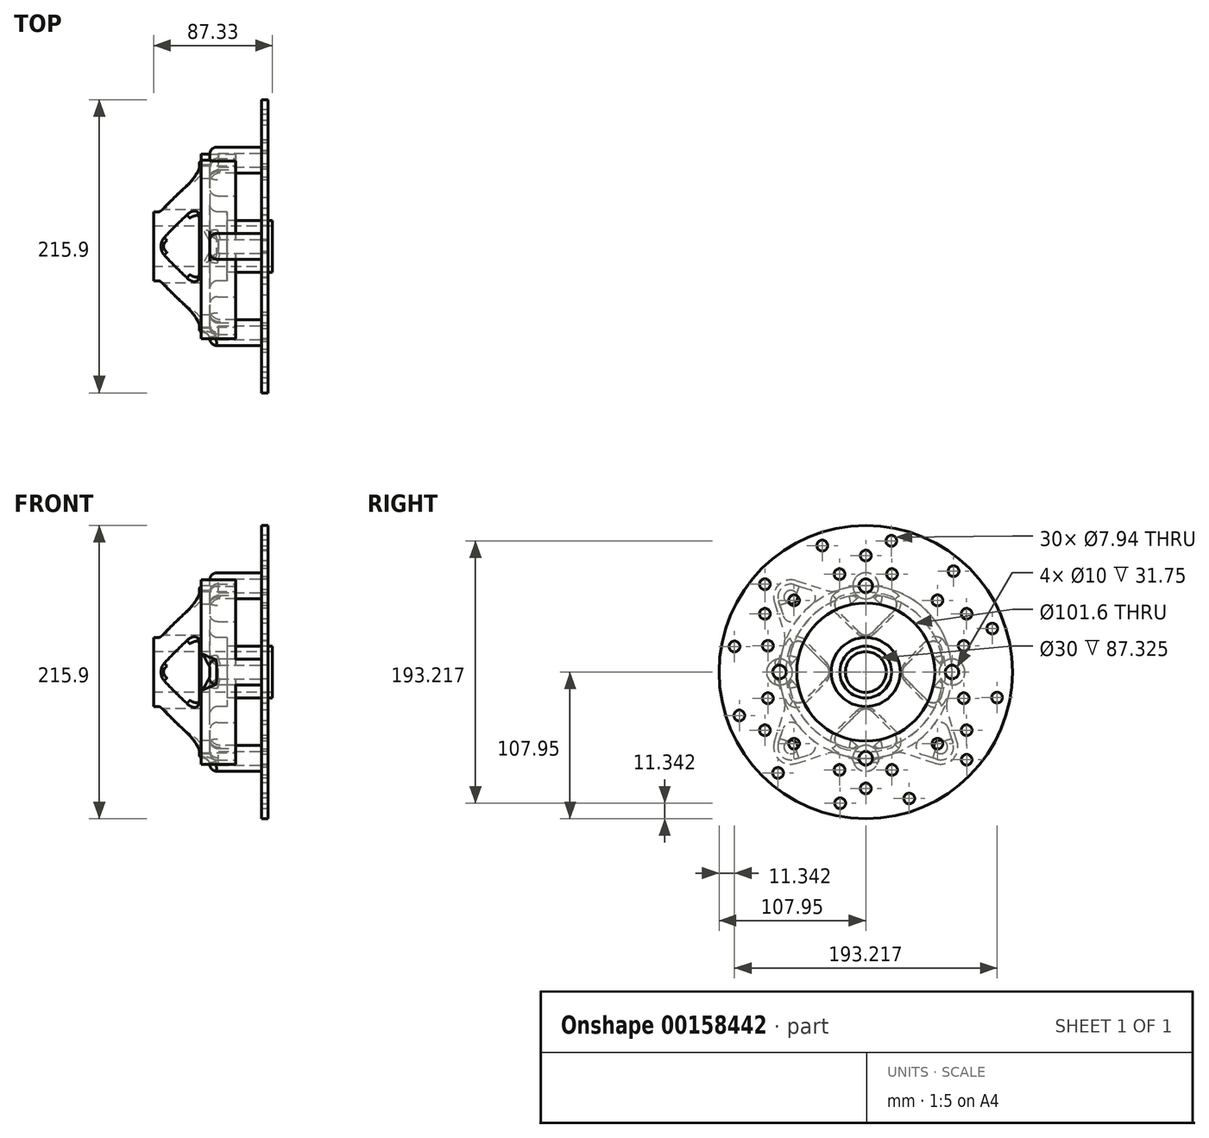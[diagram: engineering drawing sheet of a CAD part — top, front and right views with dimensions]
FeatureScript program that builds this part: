
annotation { "Feature Type Name" : "Feature", "Feature Type Description" : "" }
export const myFeature = defineFeature(function(context is Context, id is Id, definition is map)
    precondition{}
    {
        {
            var Q0;
            Q0=qCreatedBy(makeId("Front.planeOp"),FACE);
            var sketch = newSketch(context, id + "F0", { "sketchPlane" : qUnion([Q0])});
            skLineSegment(sketch, "E0", {"start": v(0, 15) * mm, "end": v(0, 25.4) * mm});
            skLineSegment(sketch, "E1", {"start": v(0, 25.4) * mm, "end": v(4.78, 25.4) * mm});
            skLineSegment(sketch, "E2", {"start": v(4.78, 25.4) * mm, "end": v(34.95, 63.5) * mm});
            skLineSegment(sketch, "E3", {"start": v(34.95, 63.5) * mm, "end": v(60.35, 63.5) * mm});
            skLineSegment(sketch, "E4", {"start": v(60.35, 63.5) * mm, "end": v(60.35, 57.15) * mm});
            skLineSegment(sketch, "E5", {"start": v(60.35, 57.15) * mm, "end": v(41.3, 57.15) * mm});
            skLineSegment(sketch, "E6", {"start": v(41.3, 57.15) * mm, "end": v(41.3, 25.4) * mm});
            skLineSegment(sketch, "E7", {"start": v(41.3, 25.4) * mm, "end": v(54, 25.4) * mm});
            skLineSegment(sketch, "E8", {"start": v(54, 25.4) * mm, "end": v(54, 19.05) * mm});
            skLineSegment(sketch, "E9", {"start": v(54, 19.05) * mm, "end": v(87.33, 19.05) * mm});
            skLineSegment(sketch, "E10", {"start": v(87.33, 19.05) * mm, "end": v(87.33, 15) * mm});
            skLineSegment(sketch, "E11", {"start": v(87.33, 15) * mm, "end": v(0, 15) * mm});
            skLineSegment(sketch, "E12", {"start": v(0, 0) * mm, "end": v(87.33, 0) * mm, "construction": true});
            skSolve(sketch);
        }
        {
            var Q0;
            Q0 = qSketchRegion(id + "F0", true);
            var Q1;
            Q1=sQuery(id+"F0.wireOp",EDGE,"E12");
            revolve(context, id + "F1", {"entities" : qUnion([Q0]), "axis" : qUnion([Q1]), "revolveType" : RevolveType.FULL});
        }
        {
            var Q0;
            Q0=makeQuery(id+"F1.opRevolve","SWEPT_FACE",FACE,{"disambiguationData":[OSD([sQuery(id+"F0.wireOp",EDGE,"E4")])]});
            var sketch = newSketch(context, id + "F2", { "sketchPlane" : qUnion([Q0])});
            skLineSegment(sketch, "E13", {"start": v(-55.15, 55.15) * mm, "end": v(55.15, 55.15) * mm, "construction": true});
            skLineSegment(sketch, "E14", {"start": v(55.15, -55.15) * mm, "end": v(55.15, 55.15) * mm, "construction": true});
            skPoint(sketch, "E15", {"position": v(55.15, 0) * mm});
            skPoint(sketch, "E16", {"position": v(0, 55.15) * mm});
            skCircle(sketch, "E17.0", {"center": v(0, 0) * mm, "radius": 63.5 * mm});
            skArc(sketch, "E18", {"start": v(51.29, 67.25) * mm, "mid": v(64.13, 64.13) * mm, "end": v(67.25, 51.29) * mm});
            skCircle(sketch, "E19", {"center": v(55.15, 55.15) * mm, "radius": 5 * mm});
            skLineSegment(sketch, "E20", {"start": v(51.29, 67.25) * mm, "end": v(28.56, 60) * mm});
            skArc(sketch, "E21", {"start": v(28.56, 60) * mm, "mid": v(24.56, 59.39) * mm, "end": v(20.58, 60.07) * mm});
            skLineSegment(sketch, "E22", {"start": v(67.25, 51.29) * mm, "end": v(60, 28.56) * mm});
            skArc(sketch, "E23", {"start": v(60, 28.56) * mm, "mid": v(59.39, 24.56) * mm, "end": v(60.07, 20.58) * mm});
            skArc(sketch, "E24.1.0", {"start": v(28.56, -60) * mm, "mid": v(24.56, -59.39) * mm, "end": v(20.58, -60.07) * mm});
            skArc(sketch, "E24.1.1", {"start": v(67.25, -51.29) * mm, "mid": v(64.13, -64.13) * mm, "end": v(51.29, -67.25) * mm});
            skLineSegment(sketch, "E24.1.2", {"start": v(67.25, -51.29) * mm, "end": v(60, -28.56) * mm});
            skArc(sketch, "E24.1.3", {"start": v(60, -28.56) * mm, "mid": v(59.39, -24.56) * mm, "end": v(60.07, -20.58) * mm});
            skCircle(sketch, "E24.1.4", {"center": v(55.15, -55.15) * mm, "radius": 5 * mm});
            skLineSegment(sketch, "E24.1.5", {"start": v(51.29, -67.25) * mm, "end": v(28.56, -60) * mm});
            skArc(sketch, "E24.2.0", {"start": v(-60, -28.56) * mm, "mid": v(-59.39, -24.56) * mm, "end": v(-60.07, -20.58) * mm});
            skArc(sketch, "E24.2.1", {"start": v(-51.29, -67.25) * mm, "mid": v(-64.13, -64.13) * mm, "end": v(-67.25, -51.29) * mm});
            skLineSegment(sketch, "E24.2.2", {"start": v(-51.29, -67.25) * mm, "end": v(-28.56, -60) * mm});
            skArc(sketch, "E24.2.3", {"start": v(-28.56, -60) * mm, "mid": v(-24.56, -59.39) * mm, "end": v(-20.58, -60.07) * mm});
            skCircle(sketch, "E24.2.4", {"center": v(-55.15, -55.15) * mm, "radius": 5 * mm});
            skLineSegment(sketch, "E24.2.5", {"start": v(-67.25, -51.29) * mm, "end": v(-60, -28.56) * mm});
            skArc(sketch, "E24.3.0", {"start": v(-28.56, 60) * mm, "mid": v(-24.56, 59.39) * mm, "end": v(-20.58, 60.07) * mm});
            skArc(sketch, "E24.3.1", {"start": v(-67.25, 51.29) * mm, "mid": v(-64.13, 64.13) * mm, "end": v(-51.29, 67.25) * mm});
            skLineSegment(sketch, "E24.3.2", {"start": v(-67.25, 51.29) * mm, "end": v(-60, 28.56) * mm});
            skArc(sketch, "E24.3.3", {"start": v(-60, 28.56) * mm, "mid": v(-59.39, 24.56) * mm, "end": v(-60.07, 20.58) * mm});
            skCircle(sketch, "E24.3.4", {"center": v(-55.15, 55.15) * mm, "radius": 5 * mm});
            skLineSegment(sketch, "E24.3.5", {"start": v(-51.29, 67.25) * mm, "end": v(-28.56, 60) * mm});
            skLineSegment(sketch, "E24.anchor1", {"start": v(0, 0) * mm, "end": v(60.07, 20.58) * mm, "construction": true});
            skLineSegment(sketch, "E24.anchor2", {"start": v(0, 0) * mm, "end": v(-20.58, 60.07) * mm, "construction": true});
            skSolve(sketch);
        }
        {
            var Q0;
            Q0=makeQuery(id+"F2.imprint","IMPRINT",FACE,{"disambiguationData":[TD([[makeQuery(id+"F2.imprint","IMPRINT",EDGE,{"derivedFrom":sQuery(id+"F2.wireOp",EDGE,"E18")}),-1.0]])]});
            var Q1;
            {var subQ0=sQuery(id+"F2.wireOp",EDGE,"E24.3.0");Q1=makeQuery(id+"F2.imprint","IMPRINT",FACE,{"disambiguationData":[TD([[makeQuery(id+"F2.imprint","IMPRINT",EDGE,{"derivedFrom":subQ0}),-1.0]])]});}
            var Q2;
            {var subQ0=sQuery(id+"F2.wireOp",EDGE,"E24.2.0");Q2=makeQuery(id+"F2.imprint","IMPRINT",FACE,{"disambiguationData":[TD([[makeQuery(id+"F2.imprint","IMPRINT",EDGE,{"derivedFrom":subQ0}),-1.0]])]});}
            var Q3;
            {var subQ1=sQuery(id+"F2.wireOp",EDGE,"E24.1.0");Q3=makeQuery(id+"F2.imprint","IMPRINT",FACE,{"disambiguationData":[TD([[makeQuery(id+"F2.imprint","IMPRINT",EDGE,{"derivedFrom":subQ1}),-1.0]])]});}
            var Q4;
            Q4=makeQuery(id+"F1.opRevolve","SWEPT_FACE",FACE,{"disambiguationData":[OSD([sQuery(id+"F0.wireOp",EDGE,"E2")])]});
            extrude(context, id + "F3", {"entities" : qUnion([Q0, Q1, Q2, Q3]), "operationType" : NewBodyOperationType.ADD, "oppositeDirection" : true, "endBoundEntityFace" : qUnion([Q4]), "depth" : 25.4 * mm});
        }
        {
            var Q0;
            Q0=makeQuery(id+"F3.opExtrude","CAP_FACE",FACE,{"disambiguationData":[OSD([sQuery(id+"F2.wireOp",EDGE,"E17.0"),sQuery(id+"F2.wireOp",EDGE,"E24.3.0"),sQuery(id+"F2.wireOp",EDGE,"E24.3.1"),sQuery(id+"F2.wireOp",EDGE,"E24.3.2"),sQuery(id+"F2.wireOp",EDGE,"E24.3.3"),sQuery(id+"F2.wireOp",EDGE,"E24.3.4"),sQuery(id+"F2.wireOp",EDGE,"E24.3.5")])],"isStart":false});
            cPlane(context, id + "F4", {"entities" : qUnion([Q0]), "cplaneType" : CPlaneType.OFFSET, "offset" : 6.35 * mm, "oppositeDirection" : true, "width" : 152.4 * mm, "height" : 152.4 * mm});
        }
        {
            var Q0;
            Q0=qCreatedBy(id+"F4.planeOp",FACE);
            var sketch = newSketch(context, id + "F5", { "sketchPlane" : qUnion([Q0])});
            skCircle(sketch, "E25", {"center": v(0, 63.5) * mm, "radius": 9.53 * mm});
            skCircle(sketch, "E26.1.0", {"center": v(-63.5, 0) * mm, "radius": 9.53 * mm});
            skCircle(sketch, "E26.2.0", {"center": v(0, -63.5) * mm, "radius": 9.53 * mm});
            skCircle(sketch, "E26.3.0", {"center": v(63.5, 0) * mm, "radius": 9.53 * mm});
            skPoint(sketch, "E26.center", {"position": v(0, 0) * mm});
            skSolve(sketch);
        }
        {
            var Q0;
            Q0 = qSketchRegion(id + "F5", true);
            extrude(context, id + "F6", {"entities" : qUnion([Q0]), "operationType" : NewBodyOperationType.ADD, "oppositeDirection" : true, "depth" : 38.1 * mm});
        }
        {
            var Q0;
            {var subQ0=sQuery(id+"F2.wireOp",EDGE,"E17.0");Q0=makeQuery(id+"F3.boolean.opBoolean","MERGE",FACE,{"derivedFrom":[makeQuery(id+"F1.opRevolve","SWEPT_FACE",FACE,{"disambiguationData":[OSD([sQuery(id+"F0.wireOp",EDGE,"E4")])]}),makeQuery(id+"F3.opExtrude","CAP_FACE",FACE,{"disambiguationData":[OSD([subQ0,sQuery(id+"F2.wireOp",EDGE,"E18"),sQuery(id+"F2.wireOp",EDGE,"E19"),sQuery(id+"F2.wireOp",EDGE,"E20"),sQuery(id+"F2.wireOp",EDGE,"E21"),sQuery(id+"F2.wireOp",EDGE,"E22"),sQuery(id+"F2.wireOp",EDGE,"E23")])],"isStart":true}),makeQuery(id+"F3.opExtrude","CAP_FACE",FACE,{"disambiguationData":[OSD([subQ0,sQuery(id+"F2.wireOp",EDGE,"E24.1.0"),sQuery(id+"F2.wireOp",EDGE,"E24.1.1"),sQuery(id+"F2.wireOp",EDGE,"E24.1.2"),sQuery(id+"F2.wireOp",EDGE,"E24.1.3"),sQuery(id+"F2.wireOp",EDGE,"E24.1.4"),sQuery(id+"F2.wireOp",EDGE,"E24.1.5")])],"isStart":true}),makeQuery(id+"F3.opExtrude","CAP_FACE",FACE,{"disambiguationData":[OSD([subQ0,sQuery(id+"F2.wireOp",EDGE,"E24.2.0"),sQuery(id+"F2.wireOp",EDGE,"E24.2.1"),sQuery(id+"F2.wireOp",EDGE,"E24.2.2"),sQuery(id+"F2.wireOp",EDGE,"E24.2.3"),sQuery(id+"F2.wireOp",EDGE,"E24.2.4"),sQuery(id+"F2.wireOp",EDGE,"E24.2.5")])],"isStart":true}),makeQuery(id+"F3.opExtrude","CAP_FACE",FACE,{"disambiguationData":[OSD([subQ0,sQuery(id+"F2.wireOp",EDGE,"E24.3.0"),sQuery(id+"F2.wireOp",EDGE,"E24.3.1"),sQuery(id+"F2.wireOp",EDGE,"E24.3.2"),sQuery(id+"F2.wireOp",EDGE,"E24.3.3"),sQuery(id+"F2.wireOp",EDGE,"E24.3.4"),sQuery(id+"F2.wireOp",EDGE,"E24.3.5")])],"isStart":true})]});}
            var sketch = newSketch(context, id + "F7", { "sketchPlane" : qUnion([Q0])});
            skLineSegment(sketch, "E27.0", {"start": v(-52.26, 64.23) * mm, "end": v(-41.47, 60.78) * mm});
            skArc(sketch, "E27.1", {"start": v(-64.23, 52.26) * mm, "mid": v(-61.89, 61.89) * mm, "end": v(-52.26, 64.23) * mm});
            skLineSegment(sketch, "E27.2", {"start": v(-64.23, 52.26) * mm, "end": v(-60.78, 41.47) * mm});
            skArc(sketch, "E28", {"start": v(-39.45, 49.76) * mm, "mid": v(-44.9, 44.9) * mm, "end": v(-49.76, 39.45) * mm});
            skArc(sketch, "E29", {"start": v(-41.47, 60.78) * mm, "mid": v(-37.15, 55.87) * mm, "end": v(-39.45, 49.76) * mm});
            skArc(sketch, "E30", {"start": v(-60.78, 41.47) * mm, "mid": v(-55.87, 37.15) * mm, "end": v(-49.76, 39.45) * mm});
            skArc(sketch, "E31.1.0", {"start": v(41.47, 60.78) * mm, "mid": v(37.15, 55.87) * mm, "end": v(39.45, 49.76) * mm});
            skArc(sketch, "E31.1.1", {"start": v(52.26, 64.23) * mm, "mid": v(61.89, 61.89) * mm, "end": v(64.23, 52.26) * mm});
            skLineSegment(sketch, "E31.1.2", {"start": v(52.26, 64.23) * mm, "end": v(41.47, 60.78) * mm});
            skLineSegment(sketch, "E31.1.3", {"start": v(64.23, 52.26) * mm, "end": v(60.78, 41.47) * mm});
            skArc(sketch, "E31.1.4", {"start": v(49.76, 39.45) * mm, "mid": v(44.9, 44.9) * mm, "end": v(39.45, 49.76) * mm});
            skArc(sketch, "E31.1.5", {"start": v(60.78, 41.47) * mm, "mid": v(55.87, 37.15) * mm, "end": v(49.76, 39.45) * mm});
            skArc(sketch, "E31.2.0", {"start": v(60.78, -41.47) * mm, "mid": v(55.87, -37.15) * mm, "end": v(49.76, -39.45) * mm});
            skArc(sketch, "E31.2.1", {"start": v(64.23, -52.26) * mm, "mid": v(61.89, -61.89) * mm, "end": v(52.26, -64.23) * mm});
            skLineSegment(sketch, "E31.2.2", {"start": v(64.23, -52.26) * mm, "end": v(60.78, -41.47) * mm});
            skLineSegment(sketch, "E31.2.3", {"start": v(52.26, -64.23) * mm, "end": v(41.47, -60.78) * mm});
            skArc(sketch, "E31.2.4", {"start": v(39.45, -49.76) * mm, "mid": v(44.9, -44.9) * mm, "end": v(49.76, -39.45) * mm});
            skArc(sketch, "E31.2.5", {"start": v(41.47, -60.78) * mm, "mid": v(37.15, -55.87) * mm, "end": v(39.45, -49.76) * mm});
            skArc(sketch, "E31.3.0", {"start": v(-41.47, -60.78) * mm, "mid": v(-37.15, -55.87) * mm, "end": v(-39.45, -49.76) * mm});
            skArc(sketch, "E31.3.1", {"start": v(-52.26, -64.23) * mm, "mid": v(-61.89, -61.89) * mm, "end": v(-64.23, -52.26) * mm});
            skLineSegment(sketch, "E31.3.2", {"start": v(-52.26, -64.23) * mm, "end": v(-41.47, -60.78) * mm});
            skLineSegment(sketch, "E31.3.3", {"start": v(-64.23, -52.26) * mm, "end": v(-60.78, -41.47) * mm});
            skArc(sketch, "E31.3.4", {"start": v(-49.76, -39.45) * mm, "mid": v(-44.9, -44.9) * mm, "end": v(-39.45, -49.76) * mm});
            skArc(sketch, "E31.3.5", {"start": v(-60.78, -41.47) * mm, "mid": v(-55.87, -37.15) * mm, "end": v(-49.76, -39.45) * mm});
            skLineSegment(sketch, "E31.anchor1", {"start": v(0, 0) * mm, "end": v(-60.78, 41.47) * mm, "construction": true});
            skLineSegment(sketch, "E31.anchor2", {"start": v(0, 0) * mm, "end": v(-41.47, -60.78) * mm, "construction": true});
            skSolve(sketch);
        }
        {
            var Q0;
            Q0 = qSketchRegion(id + "F7", true);
            var Q1;
            Q1=makeQuery(id+"F3.opExtrude","CAP_FACE",FACE,{"disambiguationData":[OSD([sQuery(id+"F2.wireOp",EDGE,"E17.0"),sQuery(id+"F2.wireOp",EDGE,"E18"),sQuery(id+"F2.wireOp",EDGE,"E19"),sQuery(id+"F2.wireOp",EDGE,"E20"),sQuery(id+"F2.wireOp",EDGE,"E21"),sQuery(id+"F2.wireOp",EDGE,"E22"),sQuery(id+"F2.wireOp",EDGE,"E23")])],"isStart":false});
            extrude(context, id + "F8", {"entities" : qUnion([Q0]), "operationType" : NewBodyOperationType.REMOVE, "oppositeDirection" : true, "endBoundEntityFace" : qUnion([Q1]), "depth" : 19.05 * mm});
        }
        {
            var Q0;
            Q0=qCreatedBy(makeId("Right.planeOp"),FACE);
            var sketch = newSketch(context, id + "F9", { "sketchPlane" : qUnion([Q0])});
            skArc(sketch, "E32", {"start": v(-4.5, 28.86) * mm, "mid": v(0, 27) * mm, "end": v(4.5, 28.86) * mm});
            skLineSegment(sketch, "E33", {"start": v(4.5, 28.86) * mm, "end": v(20.88, 45.25) * mm});
            skLineSegment(sketch, "E34", {"start": v(-4.5, 28.86) * mm, "end": v(-20.88, 45.25) * mm});
            skArc(sketch, "E35.0", {"start": v(-18.38, 55.77) * mm, "mid": v(0, 58.72) * mm, "end": v(18.38, 55.77) * mm});
            skArc(sketch, "E36", {"start": v(20.88, 45.25) * mm, "mid": v(22.57, 51.21) * mm, "end": v(18.38, 55.77) * mm});
            skArc(sketch, "E37", {"start": v(-18.38, 55.77) * mm, "mid": v(-22.57, 51.21) * mm, "end": v(-20.88, 45.25) * mm});
            skArc(sketch, "E38.1.0", {"start": v(-55.77, -18.38) * mm, "mid": v(-51.21, -22.57) * mm, "end": v(-45.25, -20.88) * mm});
            skArc(sketch, "E38.1.1", {"start": v(-45.25, 20.88) * mm, "mid": v(-51.21, 22.57) * mm, "end": v(-55.77, 18.38) * mm});
            skArc(sketch, "E38.1.2", {"start": v(-55.77, -18.38) * mm, "mid": v(-58.72, 0) * mm, "end": v(-55.77, 18.38) * mm});
            skLineSegment(sketch, "E38.1.3", {"start": v(-28.86, -4.5) * mm, "end": v(-45.25, -20.88) * mm});
            skLineSegment(sketch, "E38.1.4", {"start": v(-28.86, 4.5) * mm, "end": v(-45.25, 20.88) * mm});
            skArc(sketch, "E38.1.5", {"start": v(-28.86, -4.5) * mm, "mid": v(-27, 0) * mm, "end": v(-28.86, 4.5) * mm});
            skArc(sketch, "E38.2.0", {"start": v(18.38, -55.77) * mm, "mid": v(22.57, -51.21) * mm, "end": v(20.88, -45.25) * mm});
            skArc(sketch, "E38.2.1", {"start": v(-20.88, -45.25) * mm, "mid": v(-22.57, -51.21) * mm, "end": v(-18.38, -55.77) * mm});
            skArc(sketch, "E38.2.2", {"start": v(18.38, -55.77) * mm, "mid": v(0, -58.72) * mm, "end": v(-18.38, -55.77) * mm});
            skLineSegment(sketch, "E38.2.3", {"start": v(4.5, -28.86) * mm, "end": v(20.88, -45.25) * mm});
            skLineSegment(sketch, "E38.2.4", {"start": v(-4.5, -28.86) * mm, "end": v(-20.88, -45.25) * mm});
            skArc(sketch, "E38.2.5", {"start": v(4.5, -28.86) * mm, "mid": v(0, -27) * mm, "end": v(-4.5, -28.86) * mm});
            skArc(sketch, "E38.3.0", {"start": v(55.77, 18.38) * mm, "mid": v(51.21, 22.57) * mm, "end": v(45.25, 20.88) * mm});
            skArc(sketch, "E38.3.1", {"start": v(45.25, -20.88) * mm, "mid": v(51.21, -22.57) * mm, "end": v(55.77, -18.38) * mm});
            skArc(sketch, "E38.3.2", {"start": v(55.77, 18.38) * mm, "mid": v(58.72, 0) * mm, "end": v(55.77, -18.38) * mm});
            skLineSegment(sketch, "E38.3.3", {"start": v(28.86, 4.5) * mm, "end": v(45.25, 20.88) * mm});
            skLineSegment(sketch, "E38.3.4", {"start": v(28.86, -4.5) * mm, "end": v(45.25, -20.88) * mm});
            skArc(sketch, "E38.3.5", {"start": v(28.86, 4.5) * mm, "mid": v(27, 0) * mm, "end": v(28.86, -4.5) * mm});
            skSolve(sketch);
        }
        {
            var Q0;
            Q0 = qSketchRegion(id + "F9", true);
            var Q1;
            Q1=makeQuery(id+"F3.opExtrude","CAP_FACE",FACE,{"disambiguationData":[OSD([sQuery(id+"F2.wireOp",EDGE,"E17.0"),sQuery(id+"F2.wireOp",EDGE,"E18"),sQuery(id+"F2.wireOp",EDGE,"E19"),sQuery(id+"F2.wireOp",EDGE,"E20"),sQuery(id+"F2.wireOp",EDGE,"E21"),sQuery(id+"F2.wireOp",EDGE,"E22"),sQuery(id+"F2.wireOp",EDGE,"E23")])],"isStart":false});
            extrude(context, id + "F10", {"entities" : qUnion([Q0]), "operationType" : NewBodyOperationType.REMOVE, "endBound" : BoundingType.UP_TO_SURFACE, "endBoundEntityFace" : qUnion([Q1]), "depth" : 25.4 * mm});
        }
        {
            var Q0;
            Q0=makeQuery(id+"F6.opExtrude","CAP_FACE",FACE,{"disambiguationData":[OSD([sQuery(id+"F5.wireOp",EDGE,"E25")])],"isStart":false});
            var sketch = newSketch(context, id + "F11", { "sketchPlane" : qUnion([Q0])});
            skCircle(sketch, "E39", {"center": v(0, 63.5) * mm, "radius": 5 * mm});
            skCircle(sketch, "E40", {"center": v(63.5, 0) * mm, "radius": 5 * mm});
            skCircle(sketch, "E41", {"center": v(0, -63.5) * mm, "radius": 5 * mm});
            skCircle(sketch, "E42", {"center": v(-63.5, 0) * mm, "radius": 5 * mm});
            skSolve(sketch);
        }
        {
            var Q0;
            Q0 = qSketchRegion(id + "F11", true);
            extrude(context, id + "F12", {"entities" : qUnion([Q0]), "operationType" : NewBodyOperationType.REMOVE, "oppositeDirection" : true, "depth" : 31.75 * mm});
        }
        {
            var Q0;
            {var subQ2=sQuery(id+"F2.wireOp",EDGE,"E21");Q0=makeQuery(id+"F6.boolean.opBoolean","INTERSECT",EDGE,{"disambiguationData":[OD(0.0)],"derivedFrom":[makeQuery(id+"F3.boolean.opBoolean","SPLIT",FACE,{"disambiguationData":[TD([makeQuery(id+"F3.opExtrude","SWEPT_FACE",FACE,{"disambiguationData":[OSD([subQ2])]})])],"derivedFrom":makeQuery(id+"F1.opRevolve","SWEPT_FACE",FACE,{"disambiguationData":[OSD([sQuery(id+"F0.wireOp",EDGE,"E3")])]})}),makeQuery(id+"F6.opExtrude","SWEPT_FACE",FACE,{"disambiguationData":[OSD([sQuery(id+"F5.wireOp",EDGE,"E25")])]})]});}
            var Q1;
            {var subQ2=sQuery(id+"F2.wireOp",EDGE,"E21");Q1=makeQuery(id+"F6.boolean.opBoolean","INTERSECT",EDGE,{"disambiguationData":[OD(1.0)],"derivedFrom":[makeQuery(id+"F3.boolean.opBoolean","SPLIT",FACE,{"disambiguationData":[TD([makeQuery(id+"F3.opExtrude","SWEPT_FACE",FACE,{"disambiguationData":[OSD([subQ2])]})])],"derivedFrom":makeQuery(id+"F1.opRevolve","SWEPT_FACE",FACE,{"disambiguationData":[OSD([sQuery(id+"F0.wireOp",EDGE,"E3")])]})}),makeQuery(id+"F6.opExtrude","SWEPT_FACE",FACE,{"disambiguationData":[OSD([sQuery(id+"F5.wireOp",EDGE,"E25")])]})]});}
            var Q2;
            {var subQ2=sQuery(id+"F2.wireOp",EDGE,"E21");Q2=makeQuery(id+"F6.boolean.opBoolean","INTERSECT",EDGE,{"derivedFrom":[makeQuery(id+"F3.boolean.opBoolean","SPLIT",FACE,{"disambiguationData":[TD([makeQuery(id+"F3.opExtrude","SWEPT_FACE",FACE,{"disambiguationData":[OSD([subQ2])]})])],"derivedFrom":makeQuery(id+"F1.opRevolve","SWEPT_FACE",FACE,{"disambiguationData":[OSD([sQuery(id+"F0.wireOp",EDGE,"E3")])]})}),makeQuery(id+"F6.opExtrude","CAP_FACE",FACE,{"disambiguationData":[OSD([sQuery(id+"F5.wireOp",EDGE,"E25")])],"isStart":true})]});}
            var Q3;
            {var subQ12=sQuery(id+"F2.wireOp",EDGE,"E24.2.0");Q3=makeQuery(id+"F6.boolean.opBoolean","INTERSECT",EDGE,{"disambiguationData":[OD(1.0)],"derivedFrom":[makeQuery(id+"F3.boolean.opBoolean","SPLIT",FACE,{"disambiguationData":[TD([makeQuery(id+"F3.opExtrude","SWEPT_FACE",FACE,{"disambiguationData":[OSD([subQ12])]})])],"derivedFrom":makeQuery(id+"F1.opRevolve","SWEPT_FACE",FACE,{"disambiguationData":[OSD([sQuery(id+"F0.wireOp",EDGE,"E3")])]})}),makeQuery(id+"F6.opExtrude","SWEPT_FACE",FACE,{"disambiguationData":[OSD([sQuery(id+"F5.wireOp",EDGE,"E26.3.0")])]})]});}
            var Q4;
            {var subQ12=sQuery(id+"F2.wireOp",EDGE,"E24.2.0");Q4=makeQuery(id+"F6.boolean.opBoolean","INTERSECT",EDGE,{"derivedFrom":[makeQuery(id+"F3.boolean.opBoolean","SPLIT",FACE,{"disambiguationData":[TD([makeQuery(id+"F3.opExtrude","SWEPT_FACE",FACE,{"disambiguationData":[OSD([subQ12])]})])],"derivedFrom":makeQuery(id+"F1.opRevolve","SWEPT_FACE",FACE,{"disambiguationData":[OSD([sQuery(id+"F0.wireOp",EDGE,"E3")])]})}),makeQuery(id+"F6.opExtrude","CAP_FACE",FACE,{"disambiguationData":[OSD([sQuery(id+"F5.wireOp",EDGE,"E26.3.0")])],"isStart":true})]});}
            var Q5;
            {var subQ12=sQuery(id+"F2.wireOp",EDGE,"E24.2.0");Q5=makeQuery(id+"F6.boolean.opBoolean","INTERSECT",EDGE,{"disambiguationData":[OD(0.0)],"derivedFrom":[makeQuery(id+"F3.boolean.opBoolean","SPLIT",FACE,{"disambiguationData":[TD([makeQuery(id+"F3.opExtrude","SWEPT_FACE",FACE,{"disambiguationData":[OSD([subQ12])]})])],"derivedFrom":makeQuery(id+"F1.opRevolve","SWEPT_FACE",FACE,{"disambiguationData":[OSD([sQuery(id+"F0.wireOp",EDGE,"E3")])]})}),makeQuery(id+"F6.opExtrude","SWEPT_FACE",FACE,{"disambiguationData":[OSD([sQuery(id+"F5.wireOp",EDGE,"E26.3.0")])]})]});}
            var Q6;
            {var subQ6=sQuery(id+"F2.wireOp",EDGE,"E24.1.0");Q6=makeQuery(id+"F6.boolean.opBoolean","INTERSECT",EDGE,{"disambiguationData":[OD(1.0)],"derivedFrom":[makeQuery(id+"F3.boolean.opBoolean","SPLIT",FACE,{"disambiguationData":[TD([makeQuery(id+"F3.opExtrude","SWEPT_FACE",FACE,{"disambiguationData":[OSD([subQ6])]})])],"derivedFrom":makeQuery(id+"F1.opRevolve","SWEPT_FACE",FACE,{"disambiguationData":[OSD([sQuery(id+"F0.wireOp",EDGE,"E3")])]})}),makeQuery(id+"F6.opExtrude","SWEPT_FACE",FACE,{"disambiguationData":[OSD([sQuery(id+"F5.wireOp",EDGE,"E26.2.0")])]})]});}
            var Q7;
            {var subQ6=sQuery(id+"F2.wireOp",EDGE,"E24.1.0");Q7=makeQuery(id+"F6.boolean.opBoolean","INTERSECT",EDGE,{"derivedFrom":[makeQuery(id+"F3.boolean.opBoolean","SPLIT",FACE,{"disambiguationData":[TD([makeQuery(id+"F3.opExtrude","SWEPT_FACE",FACE,{"disambiguationData":[OSD([subQ6])]})])],"derivedFrom":makeQuery(id+"F1.opRevolve","SWEPT_FACE",FACE,{"disambiguationData":[OSD([sQuery(id+"F0.wireOp",EDGE,"E3")])]})}),makeQuery(id+"F6.opExtrude","CAP_FACE",FACE,{"disambiguationData":[OSD([sQuery(id+"F5.wireOp",EDGE,"E26.2.0")])],"isStart":true})]});}
            var Q8;
            {var subQ6=sQuery(id+"F2.wireOp",EDGE,"E24.1.0");Q8=makeQuery(id+"F6.boolean.opBoolean","INTERSECT",EDGE,{"disambiguationData":[OD(0.0)],"derivedFrom":[makeQuery(id+"F3.boolean.opBoolean","SPLIT",FACE,{"disambiguationData":[TD([makeQuery(id+"F3.opExtrude","SWEPT_FACE",FACE,{"disambiguationData":[OSD([subQ6])]})])],"derivedFrom":makeQuery(id+"F1.opRevolve","SWEPT_FACE",FACE,{"disambiguationData":[OSD([sQuery(id+"F0.wireOp",EDGE,"E3")])]})}),makeQuery(id+"F6.opExtrude","SWEPT_FACE",FACE,{"disambiguationData":[OSD([sQuery(id+"F5.wireOp",EDGE,"E26.2.0")])]})]});}
            var Q9;
            {var subQ0=sQuery(id+"F2.wireOp",EDGE,"E23");Q9=makeQuery(id+"F6.boolean.opBoolean","INTERSECT",EDGE,{"disambiguationData":[OD(1.0)],"derivedFrom":[makeQuery(id+"F3.boolean.opBoolean","SPLIT",FACE,{"disambiguationData":[TD([makeQuery(id+"F3.opExtrude","SWEPT_FACE",FACE,{"disambiguationData":[OSD([subQ0])]})])],"derivedFrom":makeQuery(id+"F1.opRevolve","SWEPT_FACE",FACE,{"disambiguationData":[OSD([sQuery(id+"F0.wireOp",EDGE,"E3")])]})}),makeQuery(id+"F6.opExtrude","SWEPT_FACE",FACE,{"disambiguationData":[OSD([sQuery(id+"F5.wireOp",EDGE,"E26.1.0")])]})]});}
            var Q10;
            {var subQ0=sQuery(id+"F2.wireOp",EDGE,"E23");Q10=makeQuery(id+"F6.boolean.opBoolean","INTERSECT",EDGE,{"derivedFrom":[makeQuery(id+"F3.boolean.opBoolean","SPLIT",FACE,{"disambiguationData":[TD([makeQuery(id+"F3.opExtrude","SWEPT_FACE",FACE,{"disambiguationData":[OSD([subQ0])]})])],"derivedFrom":makeQuery(id+"F1.opRevolve","SWEPT_FACE",FACE,{"disambiguationData":[OSD([sQuery(id+"F0.wireOp",EDGE,"E3")])]})}),makeQuery(id+"F6.opExtrude","CAP_FACE",FACE,{"disambiguationData":[OSD([sQuery(id+"F5.wireOp",EDGE,"E26.1.0")])],"isStart":true})]});}
            var Q11;
            {var subQ0=sQuery(id+"F2.wireOp",EDGE,"E23");Q11=makeQuery(id+"F6.boolean.opBoolean","INTERSECT",EDGE,{"disambiguationData":[OD(0.0)],"derivedFrom":[makeQuery(id+"F3.boolean.opBoolean","SPLIT",FACE,{"disambiguationData":[TD([makeQuery(id+"F3.opExtrude","SWEPT_FACE",FACE,{"disambiguationData":[OSD([subQ0])]})])],"derivedFrom":makeQuery(id+"F1.opRevolve","SWEPT_FACE",FACE,{"disambiguationData":[OSD([sQuery(id+"F0.wireOp",EDGE,"E3")])]})}),makeQuery(id+"F6.opExtrude","SWEPT_FACE",FACE,{"disambiguationData":[OSD([sQuery(id+"F5.wireOp",EDGE,"E26.1.0")])]})]});}
            fillet(context, id + "F13", {"entities" : qUnion([Q0, Q1, Q2, Q3, Q4, Q5, Q6, Q7, Q8, Q9, Q10, Q11]), "radius" : 5.08 * mm, "tangentPropagation" : true, "allowEdgeOverflow" : false});
        }
        {
            var Q0;
            {var subQ0=sQuery(id+"F5.wireOp",EDGE,"E25");Q0=makeQuery(id+"F6.boolean.opBoolean","SPLIT",EDGE,{"disambiguationData":[TD([makeQuery(id+"F1.opRevolve","SWEPT_FACE",FACE,{"disambiguationData":[OSD([sQuery(id+"F0.wireOp",EDGE,"E3")])]})])],"derivedFrom":makeQuery(id+"F6.opExtrude","CAP_EDGE",EDGE,{"disambiguationData":[OSD([subQ0])],"isStart":true})});}
            var Q1;
            {var subQ0=sQuery(id+"F5.wireOp",EDGE,"E26.3.0");Q1=makeQuery(id+"F6.boolean.opBoolean","SPLIT",EDGE,{"disambiguationData":[TD([makeQuery(id+"F1.opRevolve","SWEPT_FACE",FACE,{"disambiguationData":[OSD([sQuery(id+"F0.wireOp",EDGE,"E3")])]})])],"derivedFrom":makeQuery(id+"F6.opExtrude","CAP_EDGE",EDGE,{"disambiguationData":[OSD([subQ0])],"isStart":true})});}
            var Q2;
            {var subQ0=sQuery(id+"F5.wireOp",EDGE,"E26.2.0");Q2=makeQuery(id+"F6.boolean.opBoolean","SPLIT",EDGE,{"disambiguationData":[TD([makeQuery(id+"F1.opRevolve","SWEPT_FACE",FACE,{"disambiguationData":[OSD([sQuery(id+"F0.wireOp",EDGE,"E3")])]})])],"derivedFrom":makeQuery(id+"F6.opExtrude","CAP_EDGE",EDGE,{"disambiguationData":[OSD([subQ0])],"isStart":true})});}
            var Q3;
            {var subQ0=sQuery(id+"F5.wireOp",EDGE,"E26.1.0");Q3=makeQuery(id+"F6.boolean.opBoolean","SPLIT",EDGE,{"disambiguationData":[TD([makeQuery(id+"F1.opRevolve","SWEPT_FACE",FACE,{"disambiguationData":[OSD([sQuery(id+"F0.wireOp",EDGE,"E3")])]})])],"derivedFrom":makeQuery(id+"F6.opExtrude","CAP_EDGE",EDGE,{"disambiguationData":[OSD([subQ0])],"isStart":true})});}
            fillet(context, id + "F14", {"entities" : qUnion([Q0, Q1, Q2, Q3]), "radius" : 5.08 * mm, "tangentPropagation" : true, "allowEdgeOverflow" : false});
        }
        {
            var Q0;
            Q0=makeQuery(id+"F1.opRevolve","SWEPT_EDGE",EDGE,{"disambiguationData":[OSD([sQuery(id+"F0.wireOp",EDGE,"E5"),sQuery(id+"F0.wireOp",EDGE,"E6")])]});
            var Q1;
            Q1=makeQuery(id+"F1.opRevolve","SWEPT_EDGE",EDGE,{"disambiguationData":[OSD([sQuery(id+"F0.wireOp",EDGE,"E6"),sQuery(id+"F0.wireOp",EDGE,"E7")])]});
            var Q2;
            Q2=makeQuery(id+"F8.boolean.opBoolean","COPY",EDGE,{"derivedFrom":makeQuery(id+"F8.opExtrude","CAP_EDGE",EDGE,{"disambiguationData":[OSD([sQuery(id+"F7.wireOp",EDGE,"E28")])],"isStart":false})});
            var Q3;
            Q3=makeQuery(id+"F8.boolean.opBoolean","COPY",EDGE,{"derivedFrom":makeQuery(id+"F8.opExtrude","CAP_EDGE",EDGE,{"disambiguationData":[OSD([sQuery(id+"F7.wireOp",EDGE,"E31.1.3")])],"isStart":false})});
            var Q4;
            Q4=makeQuery(id+"F8.boolean.opBoolean","COPY",EDGE,{"derivedFrom":makeQuery(id+"F8.opExtrude","CAP_EDGE",EDGE,{"disambiguationData":[OSD([sQuery(id+"F7.wireOp",EDGE,"E31.2.2")])],"isStart":false})});
            var Q5;
            Q5=makeQuery(id+"F8.boolean.opBoolean","COPY",EDGE,{"derivedFrom":makeQuery(id+"F8.opExtrude","CAP_EDGE",EDGE,{"disambiguationData":[OSD([sQuery(id+"F7.wireOp",EDGE,"E31.3.0")])],"isStart":false})});
            var Q6;
            Q6=makeQuery(id+"F13.opFillet","BLEND_EDGE",EDGE,{"blendedFrom":[makeQuery(id+"F6.boolean.opBoolean","INTERSECT",EDGE,{"disambiguationData":[OD(1.0)],"derivedFrom":[makeQuery(id+"F1.opRevolve","SWEPT_FACE",FACE,{"disambiguationData":[OSD([sQuery(id+"F0.wireOp",EDGE,"E5")])]}),makeQuery(id+"F6.opExtrude","SWEPT_FACE",FACE,{"disambiguationData":[OSD([sQuery(id+"F5.wireOp",EDGE,"E25")])]})]}),makeQuery(id+"F1.opRevolve","SWEPT_FACE",FACE,{"disambiguationData":[OSD([sQuery(id+"F0.wireOp",EDGE,"E6")])]})],"blendedInto":[makeQuery(id+"F1.opRevolve","SWEPT_FACE",FACE,{"disambiguationData":[OSD([sQuery(id+"F0.wireOp",EDGE,"E6")])]})]});
            var Q7;
            Q7=makeQuery(id+"F13.opFillet","BLEND_EDGE",EDGE,{"blendedFrom":[makeQuery(id+"F6.boolean.opBoolean","INTERSECT",EDGE,{"disambiguationData":[OD(0.0)],"derivedFrom":[makeQuery(id+"F1.opRevolve","SWEPT_FACE",FACE,{"disambiguationData":[OSD([sQuery(id+"F0.wireOp",EDGE,"E5")])]}),makeQuery(id+"F6.opExtrude","SWEPT_FACE",FACE,{"disambiguationData":[OSD([sQuery(id+"F5.wireOp",EDGE,"E25")])]})]}),makeQuery(id+"F1.opRevolve","SWEPT_FACE",FACE,{"disambiguationData":[OSD([sQuery(id+"F0.wireOp",EDGE,"E6")])]})],"blendedInto":[makeQuery(id+"F1.opRevolve","SWEPT_FACE",FACE,{"disambiguationData":[OSD([sQuery(id+"F0.wireOp",EDGE,"E6")])]})]});
            fillet(context, id + "F15", {"entities" : qUnion([Q0, Q1, Q2, Q3, Q4, Q5, Q6, Q7]), "radius" : 5.7 * mm, "tangentPropagation" : true, "allowEdgeOverflow" : false});
        }
        {
            var Q0;
            Q0=makeQuery(id+"F1.opRevolve","SWEPT_EDGE",EDGE,{"disambiguationData":[OSD([sQuery(id+"F0.wireOp",EDGE,"E1"),sQuery(id+"F0.wireOp",EDGE,"E2")])]});
            var Q1;
            Q1=makeQuery(id+"F10.boolean.opBoolean","COPY",EDGE,{"derivedFrom":makeQuery(id+"F10.opExtrude","TWEAK_EDGE",EDGE,{"derivedFrom":[makeQuery(id+"F3.opExtrude","CAP_FACE",FACE,{"disambiguationData":[OSD([sQuery(id+"F2.wireOp",EDGE,"E17.0"),sQuery(id+"F2.wireOp",EDGE,"E18"),sQuery(id+"F2.wireOp",EDGE,"E19"),sQuery(id+"F2.wireOp",EDGE,"E20"),sQuery(id+"F2.wireOp",EDGE,"E21"),sQuery(id+"F2.wireOp",EDGE,"E22"),sQuery(id+"F2.wireOp",EDGE,"E23")])],"isStart":false}),makeQuery(id+"F9.imprint","IMPRINT",EDGE,{"derivedFrom":sQuery(id+"F9.wireOp",EDGE,"E38.3.4")})]})});
            var Q2;
            Q2=makeQuery(id+"F10.boolean.opBoolean","COPY",EDGE,{"derivedFrom":makeQuery(id+"F10.opExtrude","TWEAK_EDGE",EDGE,{"derivedFrom":[makeQuery(id+"F3.opExtrude","CAP_FACE",FACE,{"disambiguationData":[OSD([sQuery(id+"F2.wireOp",EDGE,"E17.0"),sQuery(id+"F2.wireOp",EDGE,"E18"),sQuery(id+"F2.wireOp",EDGE,"E19"),sQuery(id+"F2.wireOp",EDGE,"E20"),sQuery(id+"F2.wireOp",EDGE,"E21"),sQuery(id+"F2.wireOp",EDGE,"E22"),sQuery(id+"F2.wireOp",EDGE,"E23")])],"isStart":false}),makeQuery(id+"F9.imprint","IMPRINT",EDGE,{"derivedFrom":sQuery(id+"F9.wireOp",EDGE,"E38.1.3")})]})});
            var Q3;
            Q3=makeQuery(id+"F10.boolean.opBoolean","COPY",EDGE,{"derivedFrom":makeQuery(id+"F10.opExtrude","TWEAK_EDGE",EDGE,{"derivedFrom":[makeQuery(id+"F3.opExtrude","CAP_FACE",FACE,{"disambiguationData":[OSD([sQuery(id+"F2.wireOp",EDGE,"E17.0"),sQuery(id+"F2.wireOp",EDGE,"E18"),sQuery(id+"F2.wireOp",EDGE,"E19"),sQuery(id+"F2.wireOp",EDGE,"E20"),sQuery(id+"F2.wireOp",EDGE,"E21"),sQuery(id+"F2.wireOp",EDGE,"E22"),sQuery(id+"F2.wireOp",EDGE,"E23")])],"isStart":false}),makeQuery(id+"F9.imprint","IMPRINT",EDGE,{"derivedFrom":sQuery(id+"F9.wireOp",EDGE,"E33")})]})});
            var Q4;
            Q4=makeQuery(id+"F10.boolean.opBoolean","COPY",EDGE,{"derivedFrom":makeQuery(id+"F10.opExtrude","TWEAK_EDGE",EDGE,{"derivedFrom":[makeQuery(id+"F3.opExtrude","CAP_FACE",FACE,{"disambiguationData":[OSD([sQuery(id+"F2.wireOp",EDGE,"E17.0"),sQuery(id+"F2.wireOp",EDGE,"E18"),sQuery(id+"F2.wireOp",EDGE,"E19"),sQuery(id+"F2.wireOp",EDGE,"E20"),sQuery(id+"F2.wireOp",EDGE,"E21"),sQuery(id+"F2.wireOp",EDGE,"E22"),sQuery(id+"F2.wireOp",EDGE,"E23")])],"isStart":false}),makeQuery(id+"F9.imprint","IMPRINT",EDGE,{"derivedFrom":sQuery(id+"F9.wireOp",EDGE,"E38.2.3")})]})});
            fillet(context, id + "F16", {"entities" : qUnion([Q0, Q1, Q2, Q3, Q4]), "radius" : 3.17 * mm, "tangentPropagation" : true, "allowEdgeOverflow" : false});
        }
        {
            var Q0;
            Q0=makeQuery(id+"F10.boolean.opBoolean","INTERSECT",EDGE,{"derivedFrom":[makeQuery(id+"F1.opRevolve","SWEPT_FACE",FACE,{"disambiguationData":[OSD([sQuery(id+"F0.wireOp",EDGE,"E2")])]}),makeQuery(id+"F10.opExtrude","SWEPT_FACE",FACE,{"disambiguationData":[OSD([sQuery(id+"F9.wireOp",EDGE,"E38.3.3")])]})]});
            var Q1;
            Q1=makeQuery(id+"F10.boolean.opBoolean","INTERSECT",EDGE,{"derivedFrom":[makeQuery(id+"F1.opRevolve","SWEPT_FACE",FACE,{"disambiguationData":[OSD([sQuery(id+"F0.wireOp",EDGE,"E2")])]}),makeQuery(id+"F10.opExtrude","SWEPT_FACE",FACE,{"disambiguationData":[OSD([sQuery(id+"F9.wireOp",EDGE,"E38.1.3")])]})]});
            var Q2;
            Q2=makeQuery(id+"F10.boolean.opBoolean","INTERSECT",EDGE,{"derivedFrom":[makeQuery(id+"F1.opRevolve","SWEPT_FACE",FACE,{"disambiguationData":[OSD([sQuery(id+"F0.wireOp",EDGE,"E2")])]}),makeQuery(id+"F10.opExtrude","SWEPT_FACE",FACE,{"disambiguationData":[OSD([sQuery(id+"F9.wireOp",EDGE,"E38.2.4")])]})]});
            var Q3;
            Q3=makeQuery(id+"F10.boolean.opBoolean","INTERSECT",EDGE,{"derivedFrom":[makeQuery(id+"F1.opRevolve","SWEPT_FACE",FACE,{"disambiguationData":[OSD([sQuery(id+"F0.wireOp",EDGE,"E2")])]}),makeQuery(id+"F10.opExtrude","SWEPT_FACE",FACE,{"disambiguationData":[OSD([sQuery(id+"F9.wireOp",EDGE,"E33")])]})]});
            fillet(context, id + "F17", {"entities" : qUnion([Q0, Q1, Q2, Q3]), "radius" : 2.54 * mm, "tangentPropagation" : true, "allowEdgeOverflow" : false});
        }
        {
            var Q0;
            Q0=makeQuery(id+"F6.boolean.opBoolean","INTERSECT",EDGE,{"disambiguationData":[OD(0.0)],"derivedFrom":[makeQuery(id+"F1.opRevolve","SWEPT_FACE",FACE,{"disambiguationData":[OSD([sQuery(id+"F0.wireOp",EDGE,"E5")])]}),makeQuery(id+"F6.opExtrude","SWEPT_FACE",FACE,{"disambiguationData":[OSD([sQuery(id+"F5.wireOp",EDGE,"E25")])]})]});
            var Q1;
            Q1=makeQuery(id+"F6.boolean.opBoolean","INTERSECT",EDGE,{"disambiguationData":[OD(1.0)],"derivedFrom":[makeQuery(id+"F1.opRevolve","SWEPT_FACE",FACE,{"disambiguationData":[OSD([sQuery(id+"F0.wireOp",EDGE,"E5")])]}),makeQuery(id+"F6.opExtrude","SWEPT_FACE",FACE,{"disambiguationData":[OSD([sQuery(id+"F5.wireOp",EDGE,"E25")])]})]});
            var Q2;
            Q2=makeQuery(id+"F6.boolean.opBoolean","INTERSECT",EDGE,{"disambiguationData":[OD(0.0)],"derivedFrom":[makeQuery(id+"F1.opRevolve","SWEPT_FACE",FACE,{"disambiguationData":[OSD([sQuery(id+"F0.wireOp",EDGE,"E5")])]}),makeQuery(id+"F6.opExtrude","SWEPT_FACE",FACE,{"disambiguationData":[OSD([sQuery(id+"F5.wireOp",EDGE,"E26.1.0")])]})]});
            var Q3;
            Q3=makeQuery(id+"F6.boolean.opBoolean","INTERSECT",EDGE,{"disambiguationData":[OD(0.0)],"derivedFrom":[makeQuery(id+"F1.opRevolve","SWEPT_FACE",FACE,{"disambiguationData":[OSD([sQuery(id+"F0.wireOp",EDGE,"E5")])]}),makeQuery(id+"F6.opExtrude","SWEPT_FACE",FACE,{"disambiguationData":[OSD([sQuery(id+"F5.wireOp",EDGE,"E26.2.0")])]})]});
            var Q4;
            Q4=makeQuery(id+"F6.boolean.opBoolean","INTERSECT",EDGE,{"disambiguationData":[OD(1.0)],"derivedFrom":[makeQuery(id+"F1.opRevolve","SWEPT_FACE",FACE,{"disambiguationData":[OSD([sQuery(id+"F0.wireOp",EDGE,"E5")])]}),makeQuery(id+"F6.opExtrude","SWEPT_FACE",FACE,{"disambiguationData":[OSD([sQuery(id+"F5.wireOp",EDGE,"E26.3.0")])]})]});
            fillet(context, id + "F18", {"entities" : qUnion([Q0, Q1, Q2, Q3, Q4]), "radius" : 7.62 * mm, "tangentPropagation" : true, "allowEdgeOverflow" : false});
        }
        {
            var Q0;
            Q0=makeQuery(id+"F6.opExtrude","CAP_FACE",FACE,{"disambiguationData":[OSD([sQuery(id+"F5.wireOp",EDGE,"E25")])],"isStart":false});
            var sketch = newSketch(context, id + "F19", { "sketchPlane" : qUnion([Q0])});
            skCircle(sketch, "E43", {"center": v(0, 0) * mm, "radius": 50.8 * mm});
            skCircle(sketch, "E44", {"center": v(19.31, 72.07) * mm, "radius": 3.97 * mm});
            skCircle(sketch, "E45.1.0", {"center": v(-19.31, 72.07) * mm, "radius": 3.97 * mm});
            skCircle(sketch, "E45.2.0", {"center": v(-52.76, 52.76) * mm, "radius": 3.97 * mm});
            skCircle(sketch, "E45.3.0", {"center": v(-72.07, 19.31) * mm, "radius": 3.97 * mm});
            skCircle(sketch, "E45.4.0", {"center": v(-72.07, -19.31) * mm, "radius": 3.97 * mm});
            skCircle(sketch, "E45.5.0", {"center": v(-52.76, -52.76) * mm, "radius": 3.97 * mm});
            skCircle(sketch, "E45.6.0", {"center": v(-19.31, -72.07) * mm, "radius": 3.97 * mm});
            skCircle(sketch, "E45.7.0", {"center": v(19.31, -72.07) * mm, "radius": 3.97 * mm});
            skCircle(sketch, "E45.8.0", {"center": v(52.76, -52.76) * mm, "radius": 3.97 * mm});
            skCircle(sketch, "E45.9.0", {"center": v(72.07, -19.31) * mm, "radius": 3.97 * mm});
            skCircle(sketch, "E45.10.0", {"center": v(72.07, 19.31) * mm, "radius": 3.97 * mm});
            skCircle(sketch, "E45.11.0", {"center": v(52.76, 52.76) * mm, "radius": 3.97 * mm});
            skCircle(sketch, "E46", {"center": v(0, 0) * mm, "radius": 107.95 * mm});
            skLineSegment(sketch, "E47", {"start": v(-19.31, 72.07) * mm, "end": v(19.31, 72.07) * mm, "construction": true});
            skCircle(sketch, "E48", {"center": v(0, 85.73) * mm, "radius": 3.97 * mm});
            skCircle(sketch, "E49.1.0", {"center": v(-74.24, 42.86) * mm, "radius": 3.97 * mm});
            skCircle(sketch, "E49.2.0", {"center": v(-74.24, -42.86) * mm, "radius": 3.97 * mm});
            skCircle(sketch, "E49.3.0", {"center": v(0, -85.73) * mm, "radius": 3.97 * mm});
            skCircle(sketch, "E49.4.0", {"center": v(74.24, -42.86) * mm, "radius": 3.97 * mm});
            skCircle(sketch, "E49.5.0", {"center": v(74.24, 42.86) * mm, "radius": 3.97 * mm});
            skCircle(sketch, "E50", {"center": v(18.82, 96.6) * mm, "radius": 3.97 * mm});
            skCircle(sketch, "E51.1.0", {"center": v(-32, 93.08) * mm, "radius": 3.97 * mm});
            skCircle(sketch, "E51.2.0", {"center": v(-74.25, 64.6) * mm, "radius": 3.97 * mm});
            skCircle(sketch, "E51.3.0", {"center": v(-96.6, 18.82) * mm, "radius": 3.97 * mm});
            skCircle(sketch, "E51.4.0", {"center": v(-93.08, -32) * mm, "radius": 3.97 * mm});
            skCircle(sketch, "E51.5.0", {"center": v(-64.6, -74.25) * mm, "radius": 3.97 * mm});
            skCircle(sketch, "E51.6.0", {"center": v(-18.82, -96.6) * mm, "radius": 3.97 * mm});
            skCircle(sketch, "E51.7.0", {"center": v(32, -93.08) * mm, "radius": 3.97 * mm});
            skCircle(sketch, "E51.8.0", {"center": v(74.25, -64.6) * mm, "radius": 3.97 * mm});
            skCircle(sketch, "E51.9.0", {"center": v(96.6, -18.82) * mm, "radius": 3.97 * mm});
            skCircle(sketch, "E51.10.0", {"center": v(93.08, 32) * mm, "radius": 3.97 * mm});
            skCircle(sketch, "E51.11.0", {"center": v(64.6, 74.25) * mm, "radius": 3.97 * mm});
            skCircle(sketch, "E52.0", {"center": v(0, 63.5) * mm, "radius": 5 * mm});
            skCircle(sketch, "E52.1", {"center": v(-63.5, 0) * mm, "radius": 5 * mm});
            skCircle(sketch, "E52.2", {"center": v(0, -63.5) * mm, "radius": 5 * mm});
            skCircle(sketch, "E52.3", {"center": v(63.5, 0) * mm, "radius": 5 * mm});
            skSolve(sketch);
        }
        {
            var Q0;
            Q0 = qSketchRegion(id + "F19", true);
            extrude(context, id + "F20", {"entities" : qUnion([Q0]), "depth" : 4.76 * mm});
        }
    });
